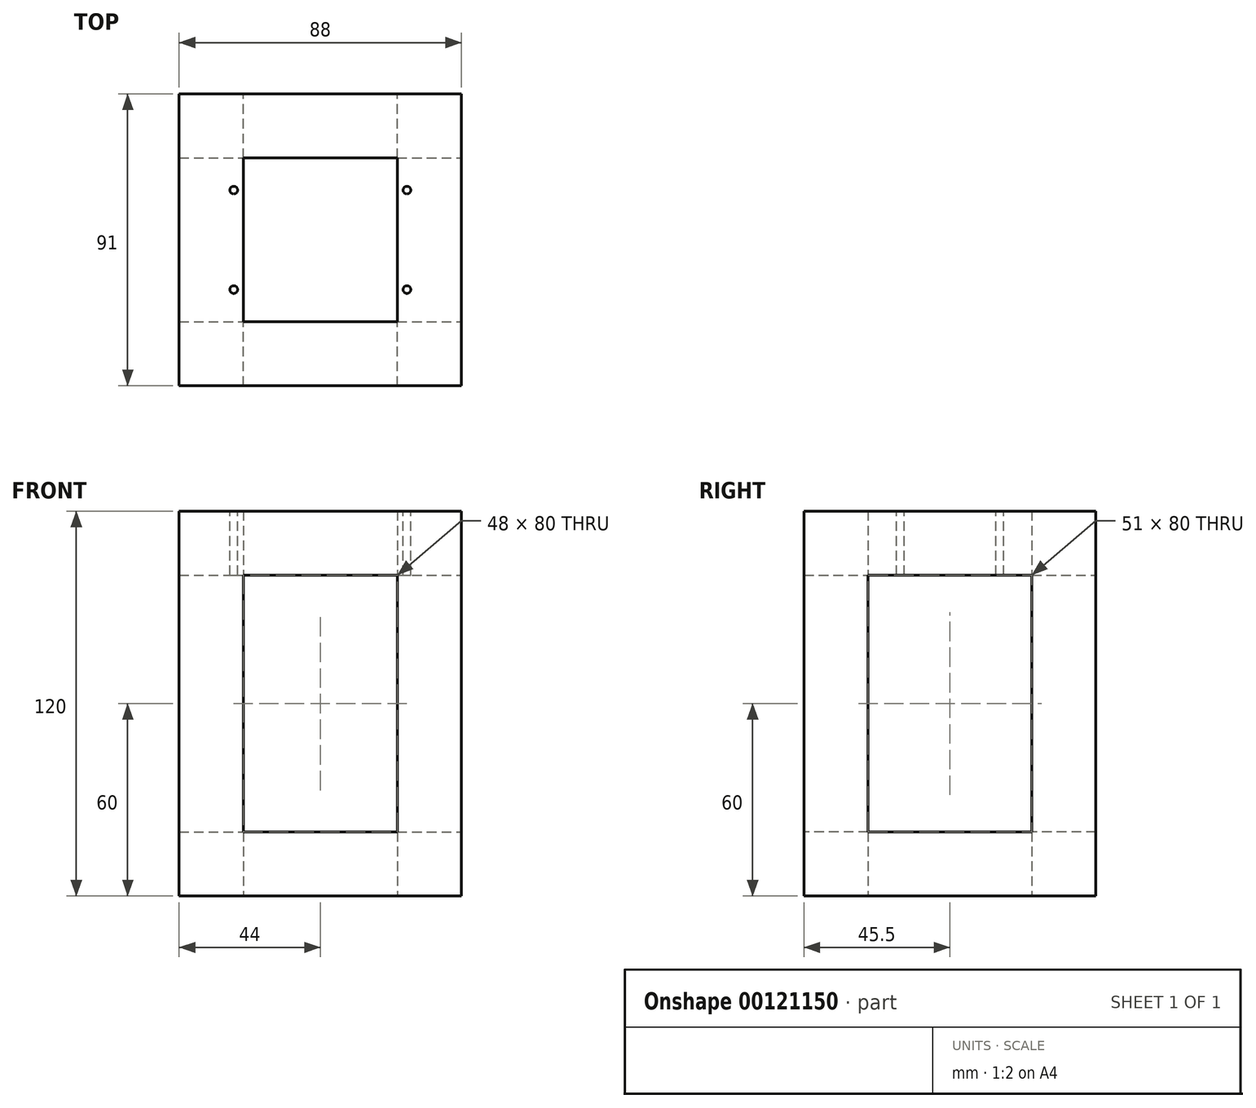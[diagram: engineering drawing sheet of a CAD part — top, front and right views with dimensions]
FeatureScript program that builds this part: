
annotation { "Feature Type Name" : "Feature", "Feature Type Description" : "" }
export const myFeature = defineFeature(function(context is Context, id is Id, definition is map)
    precondition{}
    {
        {
            var Q0;
            Q0=qCreatedBy(makeId("Top.planeOp"),FACE);
            var sketch = newSketch(context, id + "F0", { "sketchPlane" : qUnion([Q0])});
            skLineSegment(sketch, "E0", {"start": v(0, -42.91) * mm, "end": v(0, 42.3) * mm, "construction": true});
            skLineSegment(sketch, "E1", {"start": v(-57.89, 0) * mm, "end": v(53.12, 0) * mm, "construction": true});
            skLineSegment(sketch, "E2.bottom", {"start": v(44, 45.5) * mm, "end": v(-44, 45.5) * mm});
            skLineSegment(sketch, "E2.top", {"start": v(44, -45.5) * mm, "end": v(-44, -45.5) * mm});
            skLineSegment(sketch, "E2.left", {"start": v(44, 45.5) * mm, "end": v(44, -45.5) * mm});
            skLineSegment(sketch, "E2.right", {"start": v(-44, 45.5) * mm, "end": v(-44, -45.5) * mm});
            skPoint(sketch, "E2.middle", {"position": v(0, 0) * mm});
            skSolve(sketch);
        }
        {
            var Q0;
            Q0 = qSketchRegion(id + "F0", true);
            var Q1;
            Q1=makeQuery(id+"F0.imprint","IMPRINT",FACE,{"disambiguationData":[TD([[makeQuery(id+"F0.imprint","IMPRINT",EDGE,{"derivedFrom":sQuery(id+"F0.wireOp",EDGE,"E2.bottom")}),1.0]])]});
            extrude(context, id + "F1", {"entities" : qUnion([Q0, Q1]), "oppositeDirection" : true, "depth" : 20 * mm});
        }
        {
            var Q0;
            Q0=makeQuery(id+"F1.opExtrude","CAP_FACE",FACE,{"disambiguationData":[OSD([sQuery(id+"F0.wireOp",EDGE,"E2.bottom"),sQuery(id+"F0.wireOp",EDGE,"E2.top"),sQuery(id+"F0.wireOp",EDGE,"E2.left"),sQuery(id+"F0.wireOp",EDGE,"E2.right")])],"isStart":true});
            var sketch = newSketch(context, id + "F2", { "sketchPlane" : qUnion([Q0])});
            skLineSegment(sketch, "E3.bottom", {"start": v(-44, 45.5) * mm, "end": v(-24, 45.5) * mm});
            skLineSegment(sketch, "E3.top", {"start": v(-44, -45.5) * mm, "end": v(-24, -45.5) * mm});
            skLineSegment(sketch, "E3.left", {"start": v(-44, 45.5) * mm, "end": v(-44, -45.5) * mm});
            skLineSegment(sketch, "E3.right", {"start": v(-24, 45.5) * mm, "end": v(-24, -45.5) * mm});
            skLineSegment(sketch, "E4.bottom", {"start": v(44, 45.5) * mm, "end": v(24, 45.5) * mm});
            skLineSegment(sketch, "E4.top", {"start": v(44, -45.5) * mm, "end": v(24, -45.5) * mm});
            skLineSegment(sketch, "E4.left", {"start": v(44, 45.5) * mm, "end": v(44, -45.5) * mm});
            skLineSegment(sketch, "E4.right", {"start": v(24, 45.5) * mm, "end": v(24, -45.5) * mm});
            skSolve(sketch);
        }
        {
            var Q0;
            Q0 = qSketchRegion(id + "F2", true);
            extrude(context, id + "F3", {"entities" : qUnion([Q0]), "operationType" : NewBodyOperationType.ADD, "depth" : 100 * mm});
        }
        {
            var Q0;
            Q0=makeQuery(id+"F3.boolean.opBoolean","MERGE",FACE,{"derivedFrom":[makeQuery(id+"F1.opExtrude","SWEPT_FACE",FACE,{"disambiguationData":[OSD([sQuery(id+"F0.wireOp",EDGE,"E2.left")])]}),makeQuery(id+"F3.opExtrude","SWEPT_FACE",FACE,{"disambiguationData":[OSD([sQuery(id+"F2.wireOp",EDGE,"E4.left")])]})]});
            var sketch = newSketch(context, id + "F4", { "sketchPlane" : qUnion([Q0])});
            skSolve(sketch);
        }
        {
            var Q0;
            {var subQ0=sQuery(id+"F0.wireOp",EDGE,"E2.left");Q0=makeQuery(id+"F4.imprint","IMPRINT",FACE,{"disambiguationData":[TD([[makeQuery(id+"F4.imprint","IMPRINT",EDGE,{"derivedFrom":makeQuery(id+"F1.opExtrude","CAP_EDGE",EDGE,{"disambiguationData":[OSD([subQ0])],"isStart":false})}),-1.0]])]});}
            var sketch = newSketch(context, id + "F5", { "sketchPlane" : qUnion([Q0])});
            skLineSegment(sketch, "E5.bottom", {"start": v(-45.5, 100) * mm, "end": v(-25.5, 100) * mm});
            skLineSegment(sketch, "E5.top", {"start": v(-45.5, 80) * mm, "end": v(-25.5, 80) * mm});
            skLineSegment(sketch, "E5.left", {"start": v(-45.5, 100) * mm, "end": v(-45.5, 80) * mm});
            skLineSegment(sketch, "E5.right", {"start": v(-25.5, 100) * mm, "end": v(-25.5, 80) * mm});
            skLineSegment(sketch, "E6.bottom", {"start": v(25.5, 100) * mm, "end": v(45.5, 100) * mm});
            skLineSegment(sketch, "E6.top", {"start": v(25.5, 80) * mm, "end": v(45.5, 80) * mm});
            skLineSegment(sketch, "E6.left", {"start": v(25.5, 100) * mm, "end": v(25.5, 80) * mm});
            skLineSegment(sketch, "E6.right", {"start": v(45.5, 100) * mm, "end": v(45.5, 80) * mm});
            skSolve(sketch);
        }
        {
            var Q0;
            Q0 = qSketchRegion(id + "F5", true);
            extrude(context, id + "F6", {"entities" : qUnion([Q0]), "operationType" : NewBodyOperationType.ADD, "oppositeDirection" : true, "depth" : 70 * mm});
        }
        {
            var Q0;
            Q0=makeQuery(id+"F6.boolean.opBoolean","MERGE",FACE,{"derivedFrom":[makeQuery(id+"F3.opExtrude","CAP_FACE",FACE,{"disambiguationData":[OSD([sQuery(id+"F2.wireOp",EDGE,"E3.bottom"),sQuery(id+"F2.wireOp",EDGE,"E3.top"),sQuery(id+"F2.wireOp",EDGE,"E3.left"),sQuery(id+"F2.wireOp",EDGE,"E3.right")])],"isStart":false}),makeQuery(id+"F3.opExtrude","CAP_FACE",FACE,{"disambiguationData":[OSD([sQuery(id+"F2.wireOp",EDGE,"E4.bottom"),sQuery(id+"F2.wireOp",EDGE,"E4.top"),sQuery(id+"F2.wireOp",EDGE,"E4.left"),sQuery(id+"F2.wireOp",EDGE,"E4.right")])],"isStart":false}),makeQuery(id+"F6.opExtrude","SWEPT_FACE",FACE,{"disambiguationData":[OSD([sQuery(id+"F5.wireOp",EDGE,"E5.bottom")])]}),makeQuery(id+"F6.opExtrude","SWEPT_FACE",FACE,{"disambiguationData":[OSD([sQuery(id+"F5.wireOp",EDGE,"E6.bottom")])]})]});
            var sketch = newSketch(context, id + "F7", { "sketchPlane" : qUnion([Q0])});
            skCircle(sketch, "E7", {"center": v(-27, 15.5) * mm, "radius": 1.2 * mm});
            skCircle(sketch, "E8", {"center": v(-27, -15.5) * mm, "radius": 1.2 * mm});
            skCircle(sketch, "E9", {"center": v(27, 15.5) * mm, "radius": 1.2 * mm});
            skCircle(sketch, "E10", {"center": v(27, -15.5) * mm, "radius": 1.2 * mm});
            skLineSegment(sketch, "E11", {"start": v(0, 25.82) * mm, "end": v(0, -27.08) * mm, "construction": true});
            skLineSegment(sketch, "E12", {"start": v(-38.01, 0) * mm, "end": v(44.47, 0) * mm, "construction": true});
            skLineSegment(sketch, "E13", {"start": v(-32, 15.5) * mm, "end": v(49.35, 15.5) * mm, "construction": true});
            skLineSegment(sketch, "E14", {"start": v(-37.46, -15.5) * mm, "end": v(48.48, -15.5) * mm, "construction": true});
            skLineSegment(sketch, "E15", {"start": v(-27, 28.22) * mm, "end": v(-27, -25.82) * mm, "construction": true});
            skLineSegment(sketch, "E16", {"start": v(27, 25.53) * mm, "end": v(27, -23) * mm, "construction": true});
            skSolve(sketch);
        }
        {
            var Q0;
            Q0 = qSketchRegion(id + "F7", true);
            extrude(context, id + "F8", {"entities" : qUnion([Q0]), "operationType" : NewBodyOperationType.REMOVE, "oppositeDirection" : true, "depth" : 25 * mm});
        }
        {
            var Q0;
            Q0=makeQuery(id+"F1.opExtrude","CAP_FACE",FACE,{"disambiguationData":[OSD([sQuery(id+"F0.wireOp",EDGE,"E2.bottom"),sQuery(id+"F0.wireOp",EDGE,"E2.top"),sQuery(id+"F0.wireOp",EDGE,"E2.left"),sQuery(id+"F0.wireOp",EDGE,"E2.right")])],"isStart":false});
            var sketch = newSketch(context, id + "F9", { "sketchPlane" : qUnion([Q0])});
            skLineSegment(sketch, "E17.bottom", {"start": v(24, -25.5) * mm, "end": v(-24, -25.5) * mm});
            skLineSegment(sketch, "E17.top", {"start": v(24, 25.5) * mm, "end": v(-24, 25.5) * mm});
            skLineSegment(sketch, "E17.left", {"start": v(24, -25.5) * mm, "end": v(24, 25.5) * mm});
            skLineSegment(sketch, "E17.right", {"start": v(-24, -25.5) * mm, "end": v(-24, 25.5) * mm});
            skPoint(sketch, "E17.middle", {"position": v(0, 0) * mm});
            skSolve(sketch);
        }
        {
            var Q0;
            Q0 = qSketchRegion(id + "F9", true);
            extrude(context, id + "F10", {"entities" : qUnion([Q0]), "operationType" : NewBodyOperationType.REMOVE, "oppositeDirection" : true, "depth" : 25 * mm});
        }
        {
            var Q0;
            Q0=makeQuery(id+"F3.boolean.opBoolean","MERGE",FACE,{"derivedFrom":[makeQuery(id+"F1.opExtrude","SWEPT_FACE",FACE,{"disambiguationData":[OSD([sQuery(id+"F0.wireOp",EDGE,"E2.left")])]}),makeQuery(id+"F3.opExtrude","SWEPT_FACE",FACE,{"disambiguationData":[OSD([sQuery(id+"F2.wireOp",EDGE,"E4.left")])]})]});
            var sketch = newSketch(context, id + "F11", { "sketchPlane" : qUnion([Q0])});
            skLineSegment(sketch, "E18.bottom", {"start": v(-25.5, 80) * mm, "end": v(25.5, 80) * mm});
            skLineSegment(sketch, "E18.top", {"start": v(-25.5, 0) * mm, "end": v(25.5, 0) * mm});
            skLineSegment(sketch, "E18.left", {"start": v(-25.5, 80) * mm, "end": v(-25.5, 0) * mm});
            skLineSegment(sketch, "E18.right", {"start": v(25.5, 80) * mm, "end": v(25.5, 0) * mm});
            skSolve(sketch);
        }
        {
            var Q0;
            Q0 = qSketchRegion(id + "F11", true);
            extrude(context, id + "F12", {"entities" : qUnion([Q0]), "operationType" : NewBodyOperationType.REMOVE, "endBound" : BoundingType.THROUGH_ALL, "oppositeDirection" : true, "depth" : 25 * mm});
        }
    });
